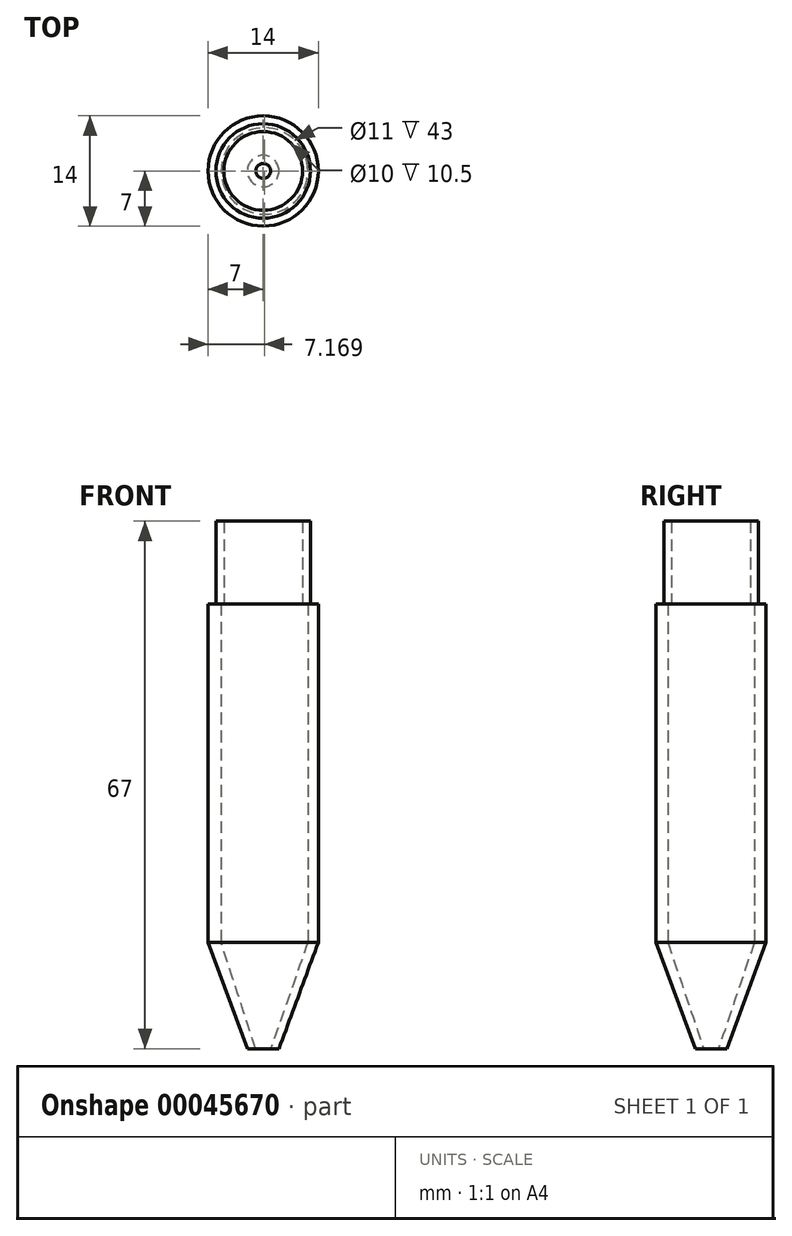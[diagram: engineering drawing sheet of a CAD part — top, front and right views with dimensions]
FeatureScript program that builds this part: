
annotation { "Feature Type Name" : "Feature", "Feature Type Description" : "" }
export const myFeature = defineFeature(function(context is Context, id is Id, definition is map)
    precondition{}
    {
        {
            var Q0;
            Q0=qCreatedBy(makeId("Top.planeOp"),FACE);
            var sketch = newSketch(context, id + "F0", { "sketchPlane" : qUnion([Q0])});
            skCircle(sketch, "E0", {"center": v(0, 0) * mm, "radius": 2 * mm});
            skSolve(sketch);
        }
        {
            var Q0;
            Q0=makeQuery(id+"F0.imprint","IMPRINT",FACE,{"disambiguationData":[TD([[makeQuery(id+"F0.imprint","IMPRINT",EDGE,{"derivedFrom":sQuery(id+"F0.wireOp",EDGE,"E0")}),1.0]])]});
            cPlane(context, id + "F1", {"entities" : qUnion([Q0]), "cplaneType" : CPlaneType.OFFSET, "offset" : 13.5 * mm, "width" : 150 * mm, "height" : 150 * mm});
        }
        {
            var Q0;
            Q0=qCreatedBy(id+"F1.planeOp",FACE);
            var sketch = newSketch(context, id + "F2", { "sketchPlane" : qUnion([Q0])});
            skCircle(sketch, "E1", {"center": v(0, 0) * mm, "radius": 7 * mm});
            skSolve(sketch);
        }
        {
            var Q0;
            Q0 = qSketchRegion(id + "F2", true);
            var Q1;
            Q1 = qSketchRegion(id + "F0", true);
            loft(context, id + "F3", {"sheetProfilesArray" : [{ "sheetProfileEntities" : qUnion([Q0]) }, { "sheetProfileEntities" : qUnion([Q1]) }]});
        }
        {
            var Q0;
            Q0=makeQuery(id+"F3.opLoft","CAP_FACE",FACE,{"disambiguationData":[OSD([makeQuery(id+"F0.imprint","IMPRINT",FACE,{"disambiguationData":[TD([[makeQuery(id+"F0.imprint","IMPRINT",EDGE,{"derivedFrom":sQuery(id+"F0.wireOp",EDGE,"E0")}),1.0]])]})])],"isStart":true});
            var sketch = newSketch(context, id + "F4", { "sketchPlane" : qUnion([Q0])});
            skCircle(sketch, "E2", {"center": v(0, 0) * mm, "radius": 0.94 * mm});
            skSolve(sketch);
        }
        {
            var Q0;
            Q0=makeQuery(id+"F3.opLoft","CAP_FACE",FACE,{"disambiguationData":[OSD([makeQuery(id+"F2.imprint","IMPRINT",FACE,{"disambiguationData":[TD([[makeQuery(id+"F2.imprint","IMPRINT",EDGE,{"derivedFrom":sQuery(id+"F2.wireOp",EDGE,"E1")}),1.0]])]})])],"isStart":true});
            var sketch = newSketch(context, id + "F5", { "sketchPlane" : qUnion([Q0])});
            skCircle(sketch, "E3", {"center": v(0.17, 0) * mm, "radius": 5.5 * mm});
            skSolve(sketch);
        }
        {
            var Q1;
            Q1 = qSketchRegion(id + "F4", true);
            var Q2;
            Q2 = qSketchRegion(id + "F5", true);
            loft(context, id + "F6", {"operationType" : NewBodyOperationType.REMOVE, "sheetProfilesArray" : [{ "sheetProfileEntities" : qUnion([Q1]) }, { "sheetProfileEntities" : qUnion([Q2]) }]});
        }
        {
            var Q0;
            Q0=makeQuery(id+"F3.opLoft","CAP_FACE",FACE,{"disambiguationData":[OSD([makeQuery(id+"F2.imprint","IMPRINT",FACE,{"disambiguationData":[TD([[makeQuery(id+"F2.imprint","IMPRINT",EDGE,{"derivedFrom":sQuery(id+"F2.wireOp",EDGE,"E1")}),1.0]])]})])],"isStart":true});
            extrude(context, id + "F7", {"entities" : qUnion([Q0]), "operationType" : NewBodyOperationType.ADD, "depth" : 43 * mm});
        }
        {
            var Q0;
            Q0=makeQuery(id+"F7.opExtrude","CAP_FACE",FACE,{"disambiguationData":[OSD([makeQuery(id+"F2.imprint","IMPRINT",FACE,{"disambiguationData":[TD([[makeQuery(id+"F2.imprint","IMPRINT",EDGE,{"derivedFrom":sQuery(id+"F2.wireOp",EDGE,"E1")}),1.0]])]})])],"isStart":false});
            var sketch = newSketch(context, id + "F8", { "sketchPlane" : qUnion([Q0])});
            skCircle(sketch, "E4", {"center": v(0, 0) * mm, "radius": 6 * mm});
            skCircle(sketch, "E5", {"center": v(0, 0) * mm, "radius": 5 * mm});
            skSolve(sketch);
        }
        {
            var Q0;
            Q0 = qSketchRegion(id + "F8", true);
            extrude(context, id + "F9", {"entities" : qUnion([Q0]), "operationType" : NewBodyOperationType.ADD, "depth" : 10.5 * mm});
        }
    });
